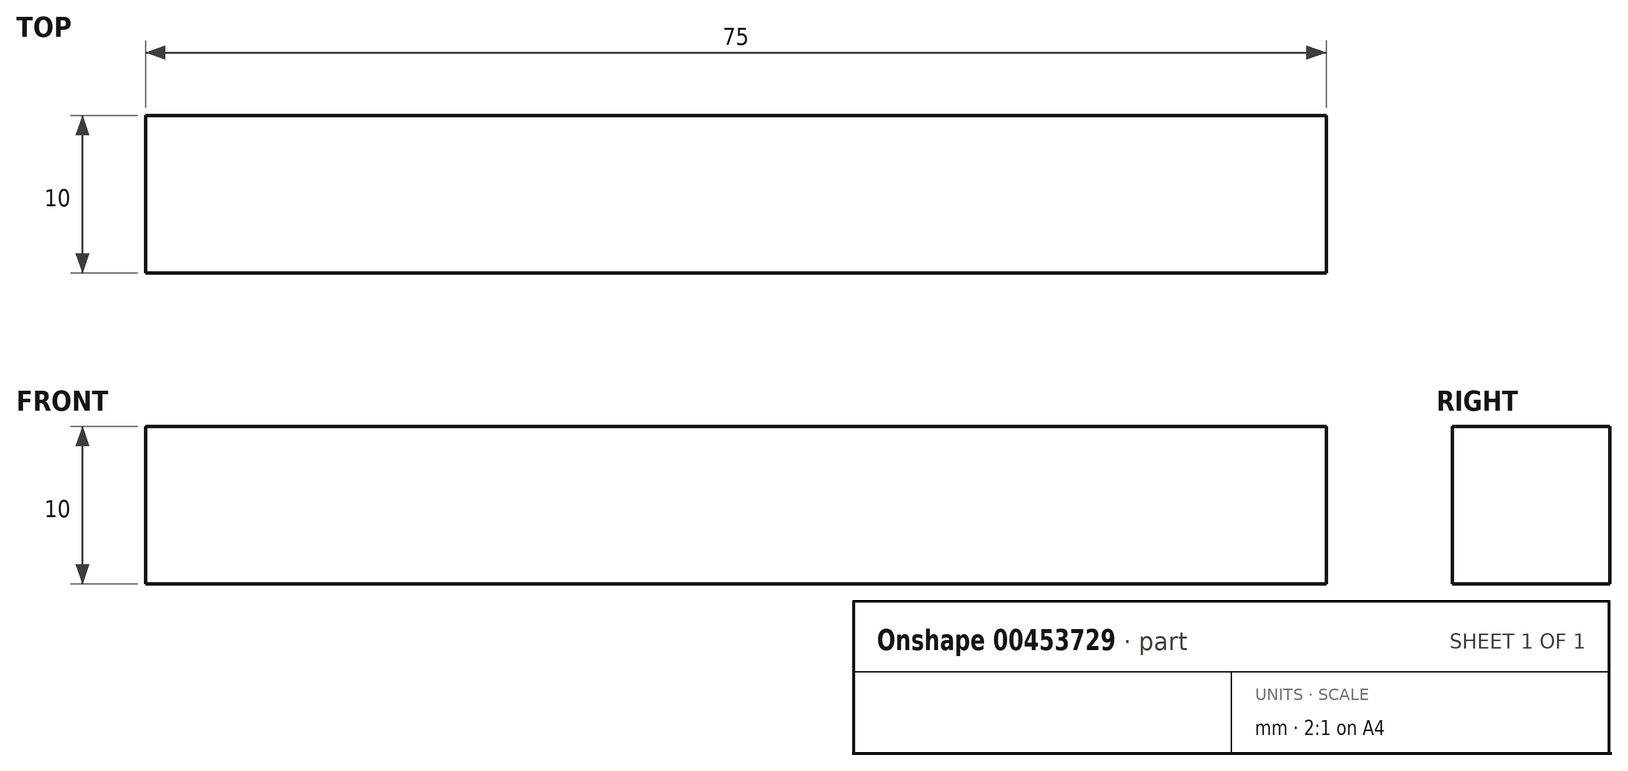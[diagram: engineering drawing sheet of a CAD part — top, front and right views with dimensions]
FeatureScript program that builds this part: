
annotation { "Feature Type Name" : "Feature", "Feature Type Description" : "" }
export const myFeature = defineFeature(function(context is Context, id is Id, definition is map)
    precondition{}
    {
        {
            var Q0;
            Q0=qCreatedBy(makeId("Top.planeOp"),FACE);
            var sketch = newSketch(context, id + "F0", { "sketchPlane" : qUnion([Q0])});
            skLineSegment(sketch, "E0.bottom", {"start": v(0, 0) * mm, "end": v(75, 0) * mm});
            skLineSegment(sketch, "E0.top", {"start": v(0, -10) * mm, "end": v(75, -10) * mm});
            skLineSegment(sketch, "E0.left", {"start": v(0, 0) * mm, "end": v(0, -10) * mm});
            skLineSegment(sketch, "E0.right", {"start": v(75, 0) * mm, "end": v(75, -10) * mm});
            skSolve(sketch);
        }
        {
            var Q0;
            Q0=makeQuery(id+"F0.imprint","IMPRINT",FACE,{"disambiguationData":[TD([[makeQuery(id+"F0.imprint","IMPRINT",EDGE,{"derivedFrom":sQuery(id+"F0.wireOp",EDGE,"E0.bottom")}),-1.0]])]});
            extrude(context, id + "F1", {"entities" : qUnion([Q0]), "oppositeDirection" : true, "depth" : 10 * mm});
        }
    });
